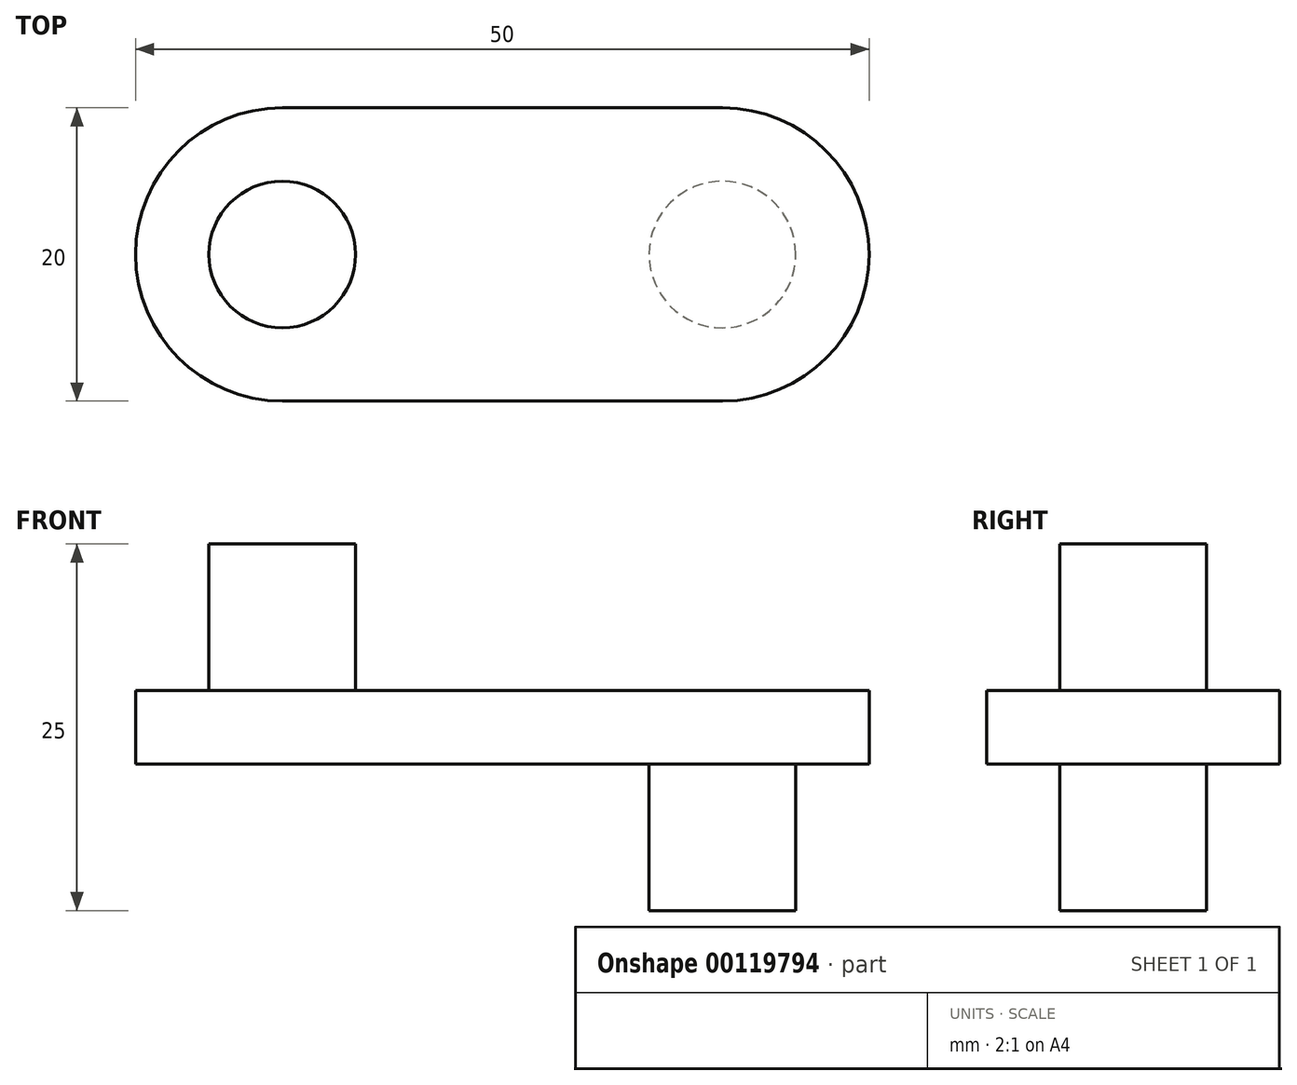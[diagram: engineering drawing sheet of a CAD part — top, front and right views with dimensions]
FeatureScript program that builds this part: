
annotation { "Feature Type Name" : "Feature", "Feature Type Description" : "" }
export const myFeature = defineFeature(function(context is Context, id is Id, definition is map)
    precondition{}
    {
        {
            var Q0;
            Q0=qCreatedBy(makeId("Top.planeOp"),FACE);
            var sketch = newSketch(context, id + "F0", { "sketchPlane" : qUnion([Q0])});
            skArc(sketch, "E0", {"start": v(0, 10) * mm, "mid": v(-10, 0) * mm, "end": v(0, -10) * mm});
            skLineSegment(sketch, "E1", {"start": v(0, 10) * mm, "end": v(30, 10) * mm});
            skLineSegment(sketch, "E2", {"start": v(0, -10) * mm, "end": v(30, -10) * mm});
            skArc(sketch, "E3", {"start": v(30, -10) * mm, "mid": v(40, 0) * mm, "end": v(30, 10) * mm});
            skSolve(sketch);
        }
        {
            var Q0;
            Q0 = qSketchRegion(id + "F0", true);
            extrude(context, id + "F1", {"entities" : qUnion([Q0]), "depth" : 5 * mm});
        }
        {
            var Q0;
            Q0=makeQuery(id+"F1.opExtrude","CAP_FACE",FACE,{"disambiguationData":[OSD([sQuery(id+"F0.wireOp",EDGE,"E0"),sQuery(id+"F0.wireOp",EDGE,"E1"),sQuery(id+"F0.wireOp",EDGE,"E2"),sQuery(id+"F0.wireOp",EDGE,"E3")])],"isStart":false});
            var sketch = newSketch(context, id + "F2", { "sketchPlane" : qUnion([Q0])});
            skCircle(sketch, "E4", {"center": v(0, 0) * mm, "radius": 5 * mm});
            skSolve(sketch);
        }
        {
            var Q0;
            Q0 = qSketchRegion(id + "F2", true);
            extrude(context, id + "F3", {"entities" : qUnion([Q0]), "operationType" : NewBodyOperationType.ADD, "depth" : 10 * mm});
        }
        {
            var Q0;
            Q0=makeQuery(id+"F1.opExtrude","CAP_FACE",FACE,{"disambiguationData":[OSD([sQuery(id+"F0.wireOp",EDGE,"E0"),sQuery(id+"F0.wireOp",EDGE,"E1"),sQuery(id+"F0.wireOp",EDGE,"E2"),sQuery(id+"F0.wireOp",EDGE,"E3")])],"isStart":true});
            var sketch = newSketch(context, id + "F4", { "sketchPlane" : qUnion([Q0])});
            skCircle(sketch, "E5", {"center": v(30, 0) * mm, "radius": 5 * mm});
            skSolve(sketch);
        }
        {
            var Q0;
            Q0 = qSketchRegion(id + "F4", true);
            extrude(context, id + "F5", {"entities" : qUnion([Q0]), "operationType" : NewBodyOperationType.ADD, "depth" : 10 * mm});
        }
    });
